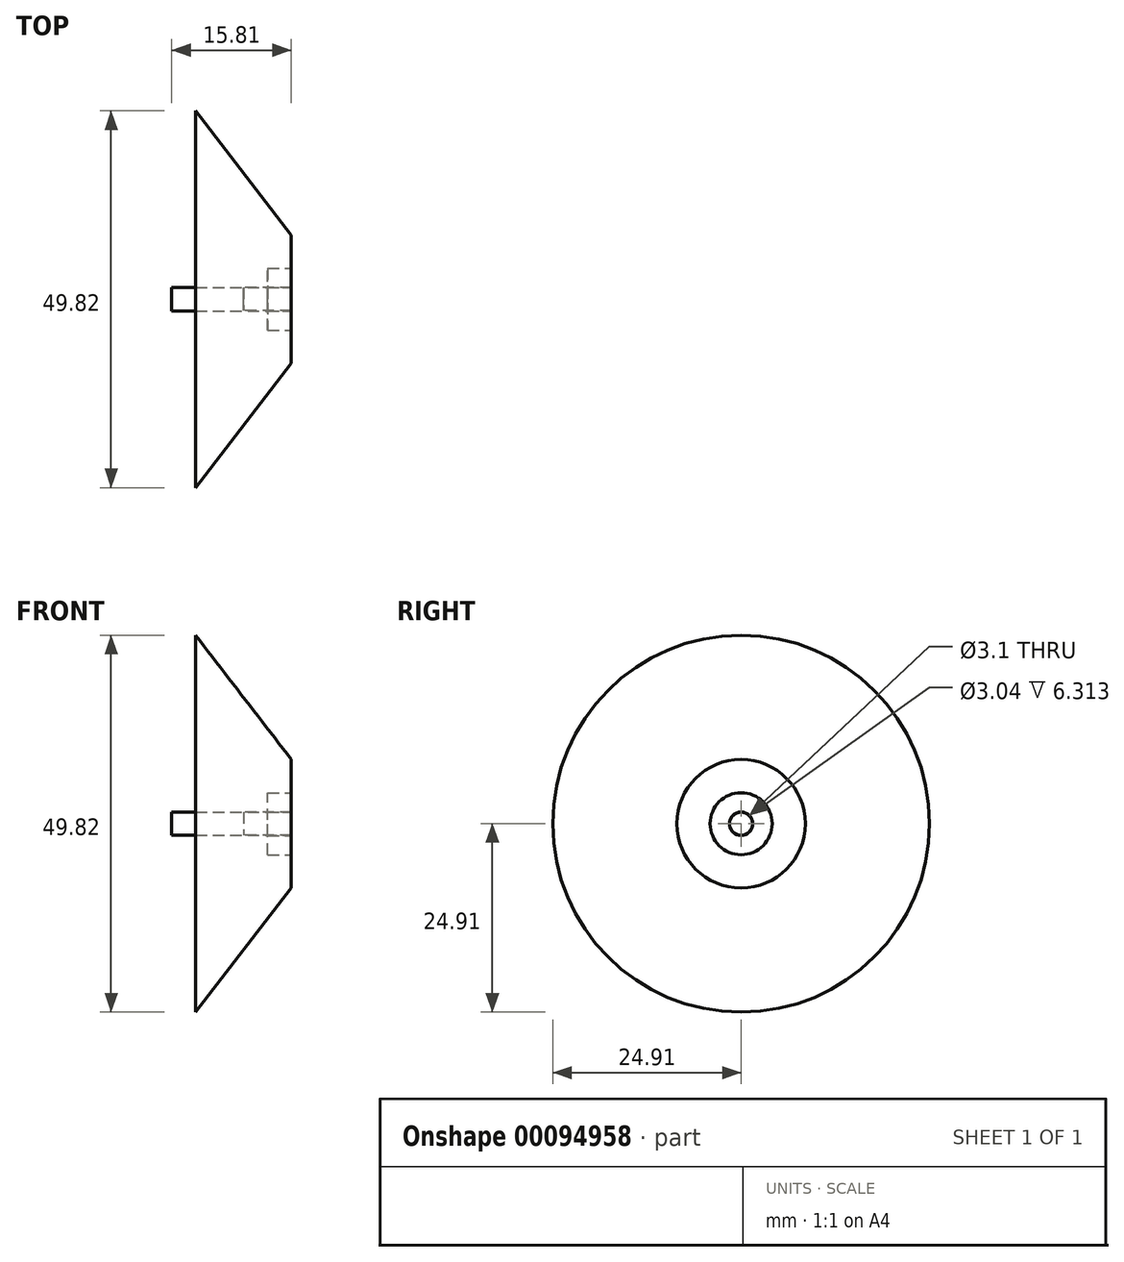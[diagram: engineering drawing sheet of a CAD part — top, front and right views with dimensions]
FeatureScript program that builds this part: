
annotation { "Feature Type Name" : "Feature", "Feature Type Description" : "" }
export const myFeature = defineFeature(function(context is Context, id is Id, definition is map)
    precondition{}
    {
        {
            var Q0;
            Q0=qCreatedBy(makeId("Front.planeOp"),FACE);
            var sketch = newSketch(context, id + "F0", { "sketchPlane" : qUnion([Q0])});
            skLineSegment(sketch, "E0", {"start": v(-12.66, 0) * mm, "end": v(-12.66, 24.9) * mm});
            skLineSegment(sketch, "E1", {"start": v(0, 8.49) * mm, "end": v(-12.66, 24.9) * mm});
            skLineSegment(sketch, "E2", {"start": v(-12.66, 0) * mm, "end": v(-6.31, 0) * mm});
            skLineSegment(sketch, "E3", {"start": v(-6.31, 0) * mm, "end": v(-6.31, 1.52) * mm});
            skLineSegment(sketch, "E4", {"start": v(-6.31, 1.52) * mm, "end": v(0, 1.52) * mm});
            skLineSegment(sketch, "E5", {"start": v(0, 1.52) * mm, "end": v(0, 8.49) * mm});
            skSolve(sketch);
        }
        {
            var Q0;
            Q0 = qSketchRegion(id + "F0", true);
            var Q1;
            Q1=sQuery(id+"F0.wireOp",EDGE,"E2");
            revolve(context, id + "F1", {"entities" : qUnion([Q0]), "axis" : qUnion([Q1]), "revolveType" : RevolveType.FULL});
        }
        {
            var Q0;
            Q0=qCreatedBy(makeId("Front.planeOp"),FACE);
            var sketch = newSketch(context, id + "F2", { "sketchPlane" : qUnion([Q0])});
            skLineSegment(sketch, "E6.bottom", {"start": v(0, 0) * mm, "end": v(-15.81, 0) * mm});
            skLineSegment(sketch, "E6.top", {"start": v(0, 1.53) * mm, "end": v(-15.81, 1.53) * mm});
            skLineSegment(sketch, "E6.left", {"start": v(0, 0) * mm, "end": v(0, 1.53) * mm});
            skLineSegment(sketch, "E6.right", {"start": v(-15.81, 0) * mm, "end": v(-15.81, 1.53) * mm});
            skSolve(sketch);
        }
        {
            var Q0;
            Q0 = qSketchRegion(id + "F2", true);
            var Q1;
            Q1=sQuery(id+"F2.wireOp",EDGE,"E6.bottom");
            revolve(context, id + "F3", {"entities" : qUnion([Q0]), "axis" : qUnion([Q1]), "revolveType" : RevolveType.FULL});
        }
        {
            var Q0;
            Q0=qCreatedBy(makeId("Front.planeOp"),FACE);
            var sketch = newSketch(context, id + "F4", { "sketchPlane" : qUnion([Q0])});
            skLineSegment(sketch, "E7.bottom", {"start": v(0, 1.55) * mm, "end": v(-3.14, 1.55) * mm});
            skLineSegment(sketch, "E7.top", {"start": v(0, 4.1) * mm, "end": v(-3.14, 4.1) * mm});
            skLineSegment(sketch, "E7.left", {"start": v(0, 1.55) * mm, "end": v(0, 4.1) * mm});
            skLineSegment(sketch, "E7.right", {"start": v(-3.14, 1.55) * mm, "end": v(-3.14, 4.1) * mm});
            skLineSegment(sketch, "E8", {"start": v(0, 0) * mm, "end": v(-3.32, 0) * mm});
            skSolve(sketch);
        }
        {
            var Q0;
            Q0 = qSketchRegion(id + "F4", true);
            var Q1;
            Q1=sQuery(id+"F4.wireOp",EDGE,"E8");
            revolve(context, id + "F5", {"entities" : qUnion([Q0]), "axis" : qUnion([Q1]), "revolveType" : RevolveType.FULL});
        }
    });
